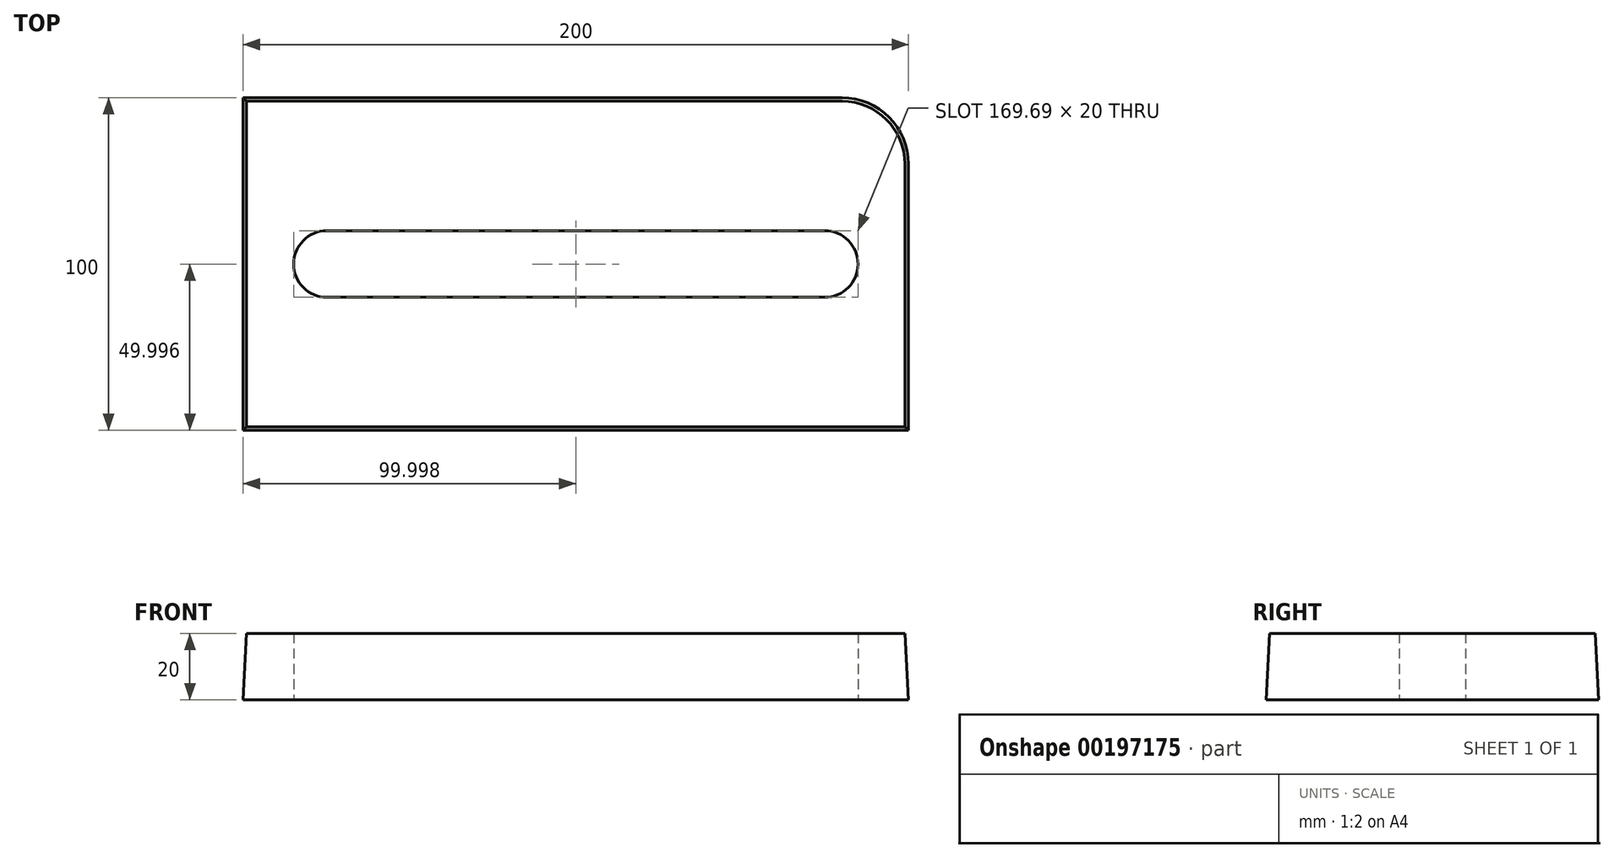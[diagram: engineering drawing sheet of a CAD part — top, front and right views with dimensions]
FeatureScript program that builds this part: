
annotation { "Feature Type Name" : "Feature", "Feature Type Description" : "" }
export const myFeature = defineFeature(function(context is Context, id is Id, definition is map)
    precondition{}
    {
        {
            var Q0;
            Q0=qCreatedBy(makeId("Top.planeOp"),FACE);
            var sketch = newSketch(context, id + "F0", { "sketchPlane" : qUnion([Q0])});
            skLineSegment(sketch, "E0.bottom", {"start": v(85.85, 214.9) * mm, "end": v(265.85, 214.9) * mm});
            skLineSegment(sketch, "E0.top", {"start": v(85.85, 114.9) * mm, "end": v(285.85, 114.9) * mm});
            skLineSegment(sketch, "E0.left", {"start": v(85.85, 214.9) * mm, "end": v(85.85, 114.9) * mm});
            skLineSegment(sketch, "E0.right", {"start": v(285.85, 194.9) * mm, "end": v(285.85, 114.9) * mm});
            skLineSegment(sketch, "E1", {"start": v(111, 164.9) * mm, "end": v(260.7, 164.9) * mm, "construction": true});
            skPoint(sketch, "E1.startSnap0", {"position": v(85.85, 164.9) * mm});
            skPoint(sketch, "E2", {"position": v(185.85, 164.9) * mm});
            skPoint(sketch, "E3", {"position": v(185.85, 114.9) * mm});
            skPoint(sketch, "E4.visualSharp", {"position": v(285.85, 214.9) * mm});
            skArc(sketch, "E4.filletArc", {"start": v(285.85, 194.9) * mm, "mid": v(280, 209.04) * mm, "end": v(265.85, 214.9) * mm});
            skArc(sketch, "E5.0.startCap", {"start": v(111, 154.9) * mm, "mid": v(101, 164.9) * mm, "end": v(111, 174.9) * mm});
            skArc(sketch, "E5.0.endCap", {"start": v(260.7, 174.9) * mm, "mid": v(270.7, 164.9) * mm, "end": v(260.7, 154.9) * mm});
            skLineSegment(sketch, "E5.0.left", {"start": v(111, 174.9) * mm, "end": v(260.7, 174.9) * mm});
            skLineSegment(sketch, "E5.0.right", {"start": v(111, 154.9) * mm, "end": v(260.7, 154.9) * mm});
            skArc(sketch, "E6.0.startCap", {"start": v(111, 159.9) * mm, "mid": v(106, 164.9) * mm, "end": v(111, 169.9) * mm});
            skArc(sketch, "E6.0.endCap", {"start": v(260.7, 169.9) * mm, "mid": v(265.7, 164.9) * mm, "end": v(260.7, 159.9) * mm});
            skLineSegment(sketch, "E6.0.left", {"start": v(111, 169.9) * mm, "end": v(260.7, 169.9) * mm});
            skLineSegment(sketch, "E6.0.right", {"start": v(111, 159.9) * mm, "end": v(260.7, 159.9) * mm});
            skSolve(sketch);
        }
        {
            var Q0;
            Q0=makeQuery(id+"F0.imprint","IMPRINT",FACE,{"disambiguationData":[TD([[makeQuery(id+"F0.imprint","IMPRINT",EDGE,{"derivedFrom":sQuery(id+"F0.wireOp",EDGE,"E0.bottom")}),-1.0]])]});
            var Q1;
            Q1=makeQuery(id+"F0.imprint","IMPRINT",FACE,{"disambiguationData":[TD([[makeQuery(id+"F0.imprint","IMPRINT",EDGE,{"derivedFrom":sQuery(id+"F0.wireOp",EDGE,"E5.0.startCap")}),-1.0]])]});
            var Q2;
            Q2=makeQuery(id+"F0.imprint","IMPRINT",FACE,{"disambiguationData":[TD([[makeQuery(id+"F0.imprint","IMPRINT",EDGE,{"derivedFrom":sQuery(id+"F0.wireOp",EDGE,"E6.0.startCap")}),-1.0]])]});
            extrude(context, id + "F1", {"entities" : qUnion([Q0, Q1, Q2]), "depth" : 30 * mm, "hasDraft" : true, "draftAngle" : 3 * degree, "draftPullDirection" : true});
        }
        {
            var Q0;
            Q0=makeQuery(id+"F0.imprint","IMPRINT",FACE,{"disambiguationData":[TD([[makeQuery(id+"F0.imprint","IMPRINT",EDGE,{"derivedFrom":sQuery(id+"F0.wireOp",EDGE,"E6.0.startCap")}),-1.0]])]});
            extrude(context, id + "F2", {"entities" : qUnion([Q0]), "operationType" : NewBodyOperationType.REMOVE, "depth" : 30 * mm});
        }
        {
            var Q0;
            Q0=makeQuery(id+"F0.imprint","IMPRINT",FACE,{"disambiguationData":[TD([[makeQuery(id+"F0.imprint","IMPRINT",EDGE,{"derivedFrom":sQuery(id+"F0.wireOp",EDGE,"E5.0.startCap")}),-1.0]])]});
            extrude(context, id + "F3", {"entities" : qUnion([Q0]), "operationType" : NewBodyOperationType.REMOVE, "depth" : 30 * mm, "hasSecondDirection" : true, "secondDirectionOppositeDirection" : false, "secondDirectionDepth" : 20 * mm});
        }
    });
